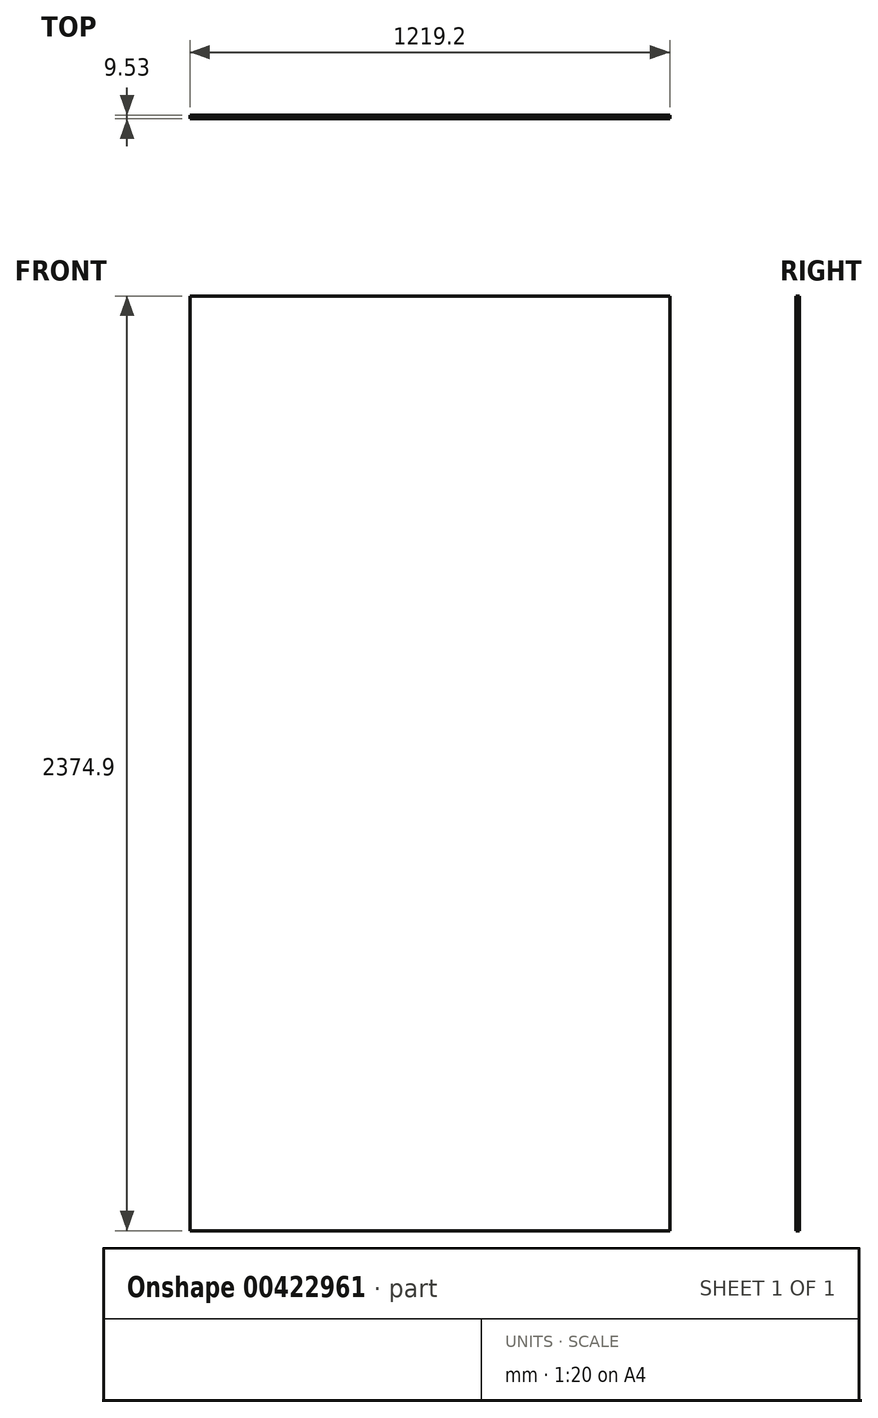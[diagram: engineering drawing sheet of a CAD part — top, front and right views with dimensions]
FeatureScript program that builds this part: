
annotation { "Feature Type Name" : "Feature", "Feature Type Description" : "" }
export const myFeature = defineFeature(function(context is Context, id is Id, definition is map)
    precondition{}
    {
        {
            var Q0;
            Q0=qCreatedBy(makeId("Front.planeOp"),FACE);
            var sketch = newSketch(context, id + "F0", { "sketchPlane" : qUnion([Q0])});
            skLineSegment(sketch, "E0.bottom", {"start": v(609.6, 1187.45) * mm, "end": v(-609.6, 1187.45) * mm});
            skLineSegment(sketch, "E0.top", {"start": v(609.6, -1187.45) * mm, "end": v(-609.6, -1187.45) * mm});
            skLineSegment(sketch, "E0.left", {"start": v(609.6, 1187.45) * mm, "end": v(609.6, -1187.45) * mm});
            skLineSegment(sketch, "E0.right", {"start": v(-609.6, 1187.45) * mm, "end": v(-609.6, -1187.45) * mm});
            skPoint(sketch, "E0.middle", {"position": v(0, 0) * mm});
            skSolve(sketch);
        }
        {
            var Q0;
            Q0 = qSketchRegion(id + "F0", true);
            extrude(context, id + "F1", {"entities" : qUnion([Q0]), "depth" : 9.52 * mm, "offsetDistance" : 25.4 * mm});
        }
    });
